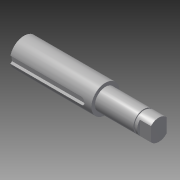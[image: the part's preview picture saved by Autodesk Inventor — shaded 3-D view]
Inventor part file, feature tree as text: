
AUTODESK INVENTOR PART (.ipt)
format: ipt  version: 2014 SP1 (Build 180222100, 222)  size: 137,216 bytes
history: native  units: in
note: dims shown in document units (in); Inventor stores cm internally (conversion verified against a paired STEP export)
features: extrude x6, sketch x5, fillet x1, chamfer x1, thread x1, plane x1
ambient origin geometry x8: Origin, YZ Plane, XZ Plane, XY Plane, X Axis, Y Axis, Z Axis, Center Point
bodies: Solid1 (feature_tree)
feature tree (15):
  sketch  "Sketch1"  dims[d0=0.5in d2=0.0625in]
  extrude  "Extrusion1"  Depth=0.5in
  extrude  "Extrusion2"  Depth=1.5in TaperAngle=0.0deg
  extrude  "Extrusion3"  Depth=0.95in TaperAngle=0.0deg
  fillet  "Fillet1"  Radius=1.375in
  chamfer  "Chamfer1"  Distance=0.05in Angle=45.0deg
  extrude  "Extrusion4"  Depth=0.5in TaperAngle=0.0deg
  thread  "Thread1"  [1 undecoded]
  extrude  "Extrusion5"  Depth=0.25in
  plane  "Work Plane1"
  extrude  "Extrusion6"  Depth=0.1969in TaperAngle=0.0deg
  sketch  "Sketch2"  dims[d3=0.125in d4=1.5in d5=0.0in]
  sketch  "Sketch3"  dims[d6=0.375in d8=0.95in d9=0.0in d10=1.375in d11=0.0in]
  sketch  "Sketch4"  dims[d12=0.0625in d13=0.05in d14=0.1in d15=45.0deg]
  sketch  "Sketch5"  dims[d16=0.185in d18=0.5in d19=0.0in d21=1.0in d22=0.0in d24=0.25in d25=0.1969in d26=0.0in d27=-0.2362in d28=0.338in d29=0.029in d30=0.0in]
note: 1 required parameter value undecoded (feature->parameter linkage not recoverable at this tier; creation-order binding heuristic only, values carry confidence <= 0.55)
